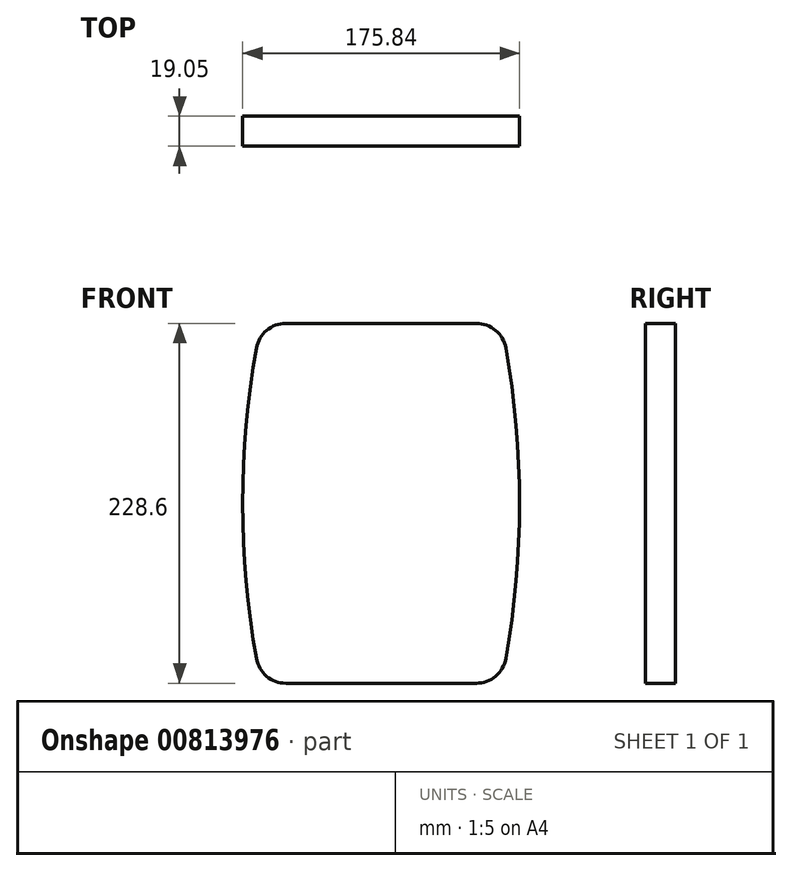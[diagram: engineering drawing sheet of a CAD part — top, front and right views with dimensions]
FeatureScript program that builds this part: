
annotation { "Feature Type Name" : "Feature", "Feature Type Description" : "" }
export const myFeature = defineFeature(function(context is Context, id is Id, definition is map)
    precondition{}
    {
        {
            var Q0;
            Q0=qCreatedBy(makeId("Front.planeOp"),FACE);
            var sketch = newSketch(context, id + "F0", { "sketchPlane" : qUnion([Q0])});
            skLineSegment(sketch, "E0.bottom", {"start": v(-113.87, 161.68) * mm, "end": v(38.53, 161.68) * mm});
            skLineSegment(sketch, "E0.top", {"start": v(-113.87, -66.92) * mm, "end": v(38.53, -66.92) * mm});
            skLineSegment(sketch, "E0.left", {"start": v(-113.87, 161.68) * mm, "end": v(-113.87, -66.92) * mm});
            skLineSegment(sketch, "E0.right", {"start": v(38.53, 161.68) * mm, "end": v(38.53, -66.92) * mm});
            skArc(sketch, "E1", {"start": v(-113.87, 161.68) * mm, "mid": v(-125.59, 47.38) * mm, "end": v(-113.87, -66.92) * mm});
            skArc(sketch, "E2", {"start": v(38.53, -66.92) * mm, "mid": v(50.25, 47.38) * mm, "end": v(38.53, 161.68) * mm});
            skLineSegment(sketch, "E3.top", {"start": v(-99.34, -66.92) * mm, "end": v(-92.99, -66.92) * mm});
            skLineSegment(sketch, "E4.top", {"start": v(-81.62, -66.92) * mm, "end": v(-75.27, -66.92) * mm});
            skLineSegment(sketch, "E5.top", {"start": v(-113.87, -66.92) * mm, "end": v(-99.34, -66.92) * mm});
            skLineSegment(sketch, "E6.bottom", {"start": v(-92.99, 161.68) * mm, "end": v(-81.62, 161.68) * mm});
            skLineSegment(sketch, "E6.top", {"start": v(-92.99, -66.92) * mm, "end": v(-81.62, -66.92) * mm});
            skSolve(sketch);
        }
        {
            var Q0;
            Q0=makeQuery(id+"F0.imprint","IMPRINT",FACE,{"disambiguationData":[TD([[makeQuery(id+"F0.imprint","IMPRINT",EDGE,{"derivedFrom":sQuery(id+"F0.wireOp",EDGE,"E0.bottom")}),-1.0]])]});
            extrude(context, id + "F1", {"entities" : qUnion([Q0]), "depth" : 19.05 * mm, "offsetDistance" : 25.4 * mm});
        }
        {
            var Q0;
            Q0=makeQuery(id+"F0.imprint","IMPRINT",FACE,{"disambiguationData":[TD([[makeQuery(id+"F0.imprint","IMPRINT",EDGE,{"derivedFrom":sQuery(id+"F0.wireOp",EDGE,"E0.left")}),-1.0]])]});
            extrude(context, id + "F2", {"entities" : qUnion([Q0]), "operationType" : NewBodyOperationType.ADD, "depth" : 19.05 * mm, "offsetDistance" : 25.4 * mm});
        }
        {
            var Q0;
            Q0=makeQuery(id+"F0.imprint","IMPRINT",FACE,{"disambiguationData":[TD([[makeQuery(id+"F0.imprint","IMPRINT",EDGE,{"derivedFrom":sQuery(id+"F0.wireOp",EDGE,"E0.right")}),1.0]])]});
            extrude(context, id + "F3", {"entities" : qUnion([Q0]), "operationType" : NewBodyOperationType.ADD, "depth" : 19.05 * mm, "offsetDistance" : 25.4 * mm});
        }
        {
            var Q0;
            {var subQ0=sQuery(id+"F0.wireOp",EDGE,"E1");var subQ1=sQuery(id+"F0.wireOp",EDGE,"E0.left");var subQ2=sQuery(id+"F0.wireOp",EDGE,"E0.bottom");Q0=makeQuery(id+"F2.boolean.opBoolean","MERGE",EDGE,{"derivedFrom":[makeQuery(id+"F1.opExtrude","SWEPT_EDGE",EDGE,{"disambiguationData":[OSD([subQ2,subQ1,subQ0])]}),makeQuery(id+"F2.opExtrude","SWEPT_EDGE",EDGE,{"disambiguationData":[OSD([subQ2,subQ1,subQ0])]})]});}
            var Q1;
            {var subQ0=sQuery(id+"F0.wireOp",EDGE,"E2");var subQ1=sQuery(id+"F0.wireOp",EDGE,"E0.right");var subQ2=sQuery(id+"F0.wireOp",EDGE,"E0.bottom");Q1=makeQuery(id+"F3.boolean.opBoolean","MERGE",EDGE,{"derivedFrom":[makeQuery(id+"F1.opExtrude","SWEPT_EDGE",EDGE,{"disambiguationData":[OSD([subQ2,subQ1,subQ0])]}),makeQuery(id+"F3.opExtrude","SWEPT_EDGE",EDGE,{"disambiguationData":[OSD([subQ2,subQ1,subQ0])]})]});}
            var Q2;
            {var subQ0=sQuery(id+"F0.wireOp",EDGE,"E2");var subQ1=sQuery(id+"F0.wireOp",EDGE,"E0.right");var subQ2=sQuery(id+"F0.wireOp",EDGE,"E0.top");Q2=makeQuery(id+"F3.boolean.opBoolean","MERGE",EDGE,{"derivedFrom":[makeQuery(id+"F1.opExtrude","SWEPT_EDGE",EDGE,{"disambiguationData":[OSD([subQ2,subQ1,subQ0])]}),makeQuery(id+"F3.opExtrude","SWEPT_EDGE",EDGE,{"disambiguationData":[OSD([subQ2,subQ1,subQ0])]})]});}
            var Q3;
            {var subQ0=sQuery(id+"F0.wireOp",EDGE,"E1");var subQ1=sQuery(id+"F0.wireOp",EDGE,"E0.left");var subQ2=sQuery(id+"F0.wireOp",EDGE,"E0.top");Q3=makeQuery(id+"F2.boolean.opBoolean","MERGE",EDGE,{"derivedFrom":[makeQuery(id+"F1.opExtrude","SWEPT_EDGE",EDGE,{"disambiguationData":[OSD([subQ2,subQ1,subQ0])]}),makeQuery(id+"F2.opExtrude","SWEPT_EDGE",EDGE,{"disambiguationData":[OSD([subQ2,subQ1,subQ0])]})]});}
            fillet(context, id + "F4", {"entities" : qUnion([Q0, Q1, Q2, Q3]), "radius" : 19.05 * mm, "tangentPropagation" : true, "allowEdgeOverflow" : false});
        }
    });
